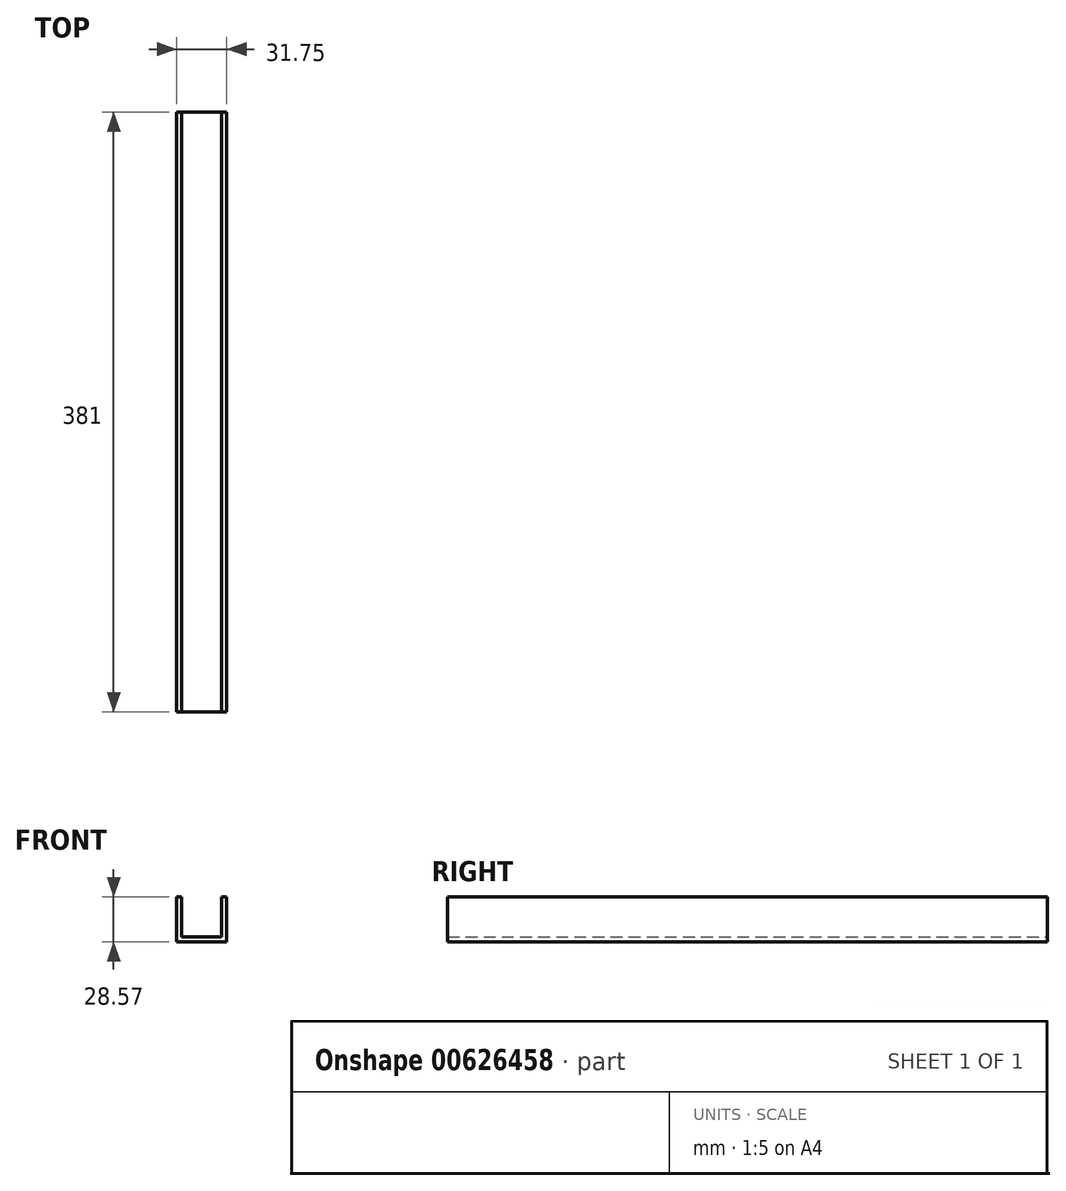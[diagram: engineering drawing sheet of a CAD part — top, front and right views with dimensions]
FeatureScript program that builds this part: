
annotation { "Feature Type Name" : "Feature", "Feature Type Description" : "" }
export const myFeature = defineFeature(function(context is Context, id is Id, definition is map)
    precondition{}
    {
        {
            var Q0;
            Q0=qCreatedBy(makeId("Front.planeOp"),FACE);
            var sketch = newSketch(context, id + "F0", { "sketchPlane" : qUnion([Q0])});
            skLineSegment(sketch, "E0", {"start": v(0, 0) * mm, "end": v(31.75, 0) * mm});
            skLineSegment(sketch, "E1", {"start": v(31.75, 0) * mm, "end": v(31.75, 28.58) * mm});
            skLineSegment(sketch, "E2", {"start": v(31.75, 28.58) * mm, "end": v(28.57, 28.58) * mm});
            skLineSegment(sketch, "E3", {"start": v(28.57, 28.58) * mm, "end": v(28.57, 3.18) * mm});
            skLineSegment(sketch, "E4", {"start": v(28.58, 3.18) * mm, "end": v(3.18, 3.17) * mm});
            skLineSegment(sketch, "E5", {"start": v(3.18, 3.18) * mm, "end": v(3.18, 28.58) * mm});
            skLineSegment(sketch, "E6", {"start": v(3.18, 28.58) * mm, "end": v(0, 28.58) * mm});
            skLineSegment(sketch, "E7", {"start": v(0, 28.58) * mm, "end": v(0, 0) * mm});
            skSolve(sketch);
        }
        {
            var Q0;
            Q0=makeQuery(id+"F0.imprint","IMPRINT",FACE,{"disambiguationData":[TD([[makeQuery(id+"F0.imprint","IMPRINT",EDGE,{"derivedFrom":sQuery(id+"F0.wireOp",EDGE,"E0")}),1.0]])]});
            extrude(context, id + "F1", {"entities" : qUnion([Q0]), "depth" : 381 * mm, "offsetDistance" : 25.4 * mm});
        }
    });
